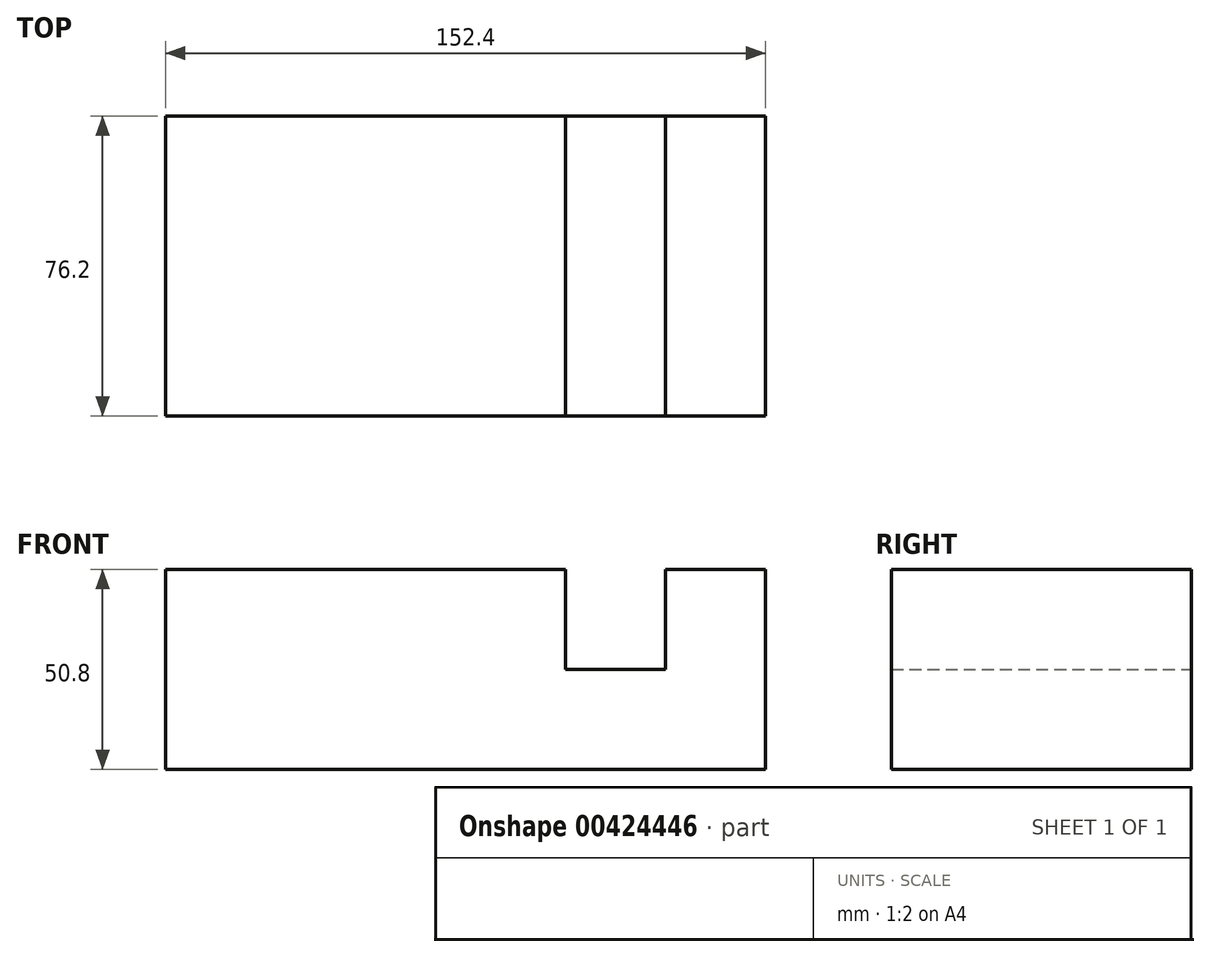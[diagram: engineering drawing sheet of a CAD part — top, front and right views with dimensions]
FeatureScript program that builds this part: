
annotation { "Feature Type Name" : "Feature", "Feature Type Description" : "" }
export const myFeature = defineFeature(function(context is Context, id is Id, definition is map)
    precondition{}
    {
        {
            var Q0;
            Q0=qCreatedBy(makeId("Front.planeOp"),FACE);
            var sketch = newSketch(context, id + "F0", { "sketchPlane" : qUnion([Q0])});
            skLineSegment(sketch, "E0", {"start": v(0, 0) * mm, "end": v(0, 50.8) * mm});
            skLineSegment(sketch, "E1", {"start": v(0, 50.8) * mm, "end": v(101.6, 50.8) * mm});
            skLineSegment(sketch, "E2", {"start": v(101.6, 50.8) * mm, "end": v(101.6, 25.4) * mm});
            skLineSegment(sketch, "E3", {"start": v(101.6, 25.4) * mm, "end": v(127, 25.4) * mm});
            skLineSegment(sketch, "E4", {"start": v(127, 25.4) * mm, "end": v(127, 50.8) * mm});
            skLineSegment(sketch, "E5", {"start": v(127, 50.8) * mm, "end": v(152.4, 50.8) * mm});
            skLineSegment(sketch, "E6", {"start": v(152.4, 50.8) * mm, "end": v(152.4, 0) * mm});
            skLineSegment(sketch, "E7", {"start": v(152.4, 0) * mm, "end": v(0, 0) * mm});
            skSolve(sketch);
        }
        {
            var Q0;
            Q0=makeQuery(id+"F0.imprint","IMPRINT",FACE,{"disambiguationData":[TD([[makeQuery(id+"F0.imprint","IMPRINT",EDGE,{"derivedFrom":sQuery(id+"F0.wireOp",EDGE,"E0")}),-1.0]])]});
            extrude(context, id + "F1", {"entities" : qUnion([Q0]), "depth" : 76.2 * mm});
        }
    });
